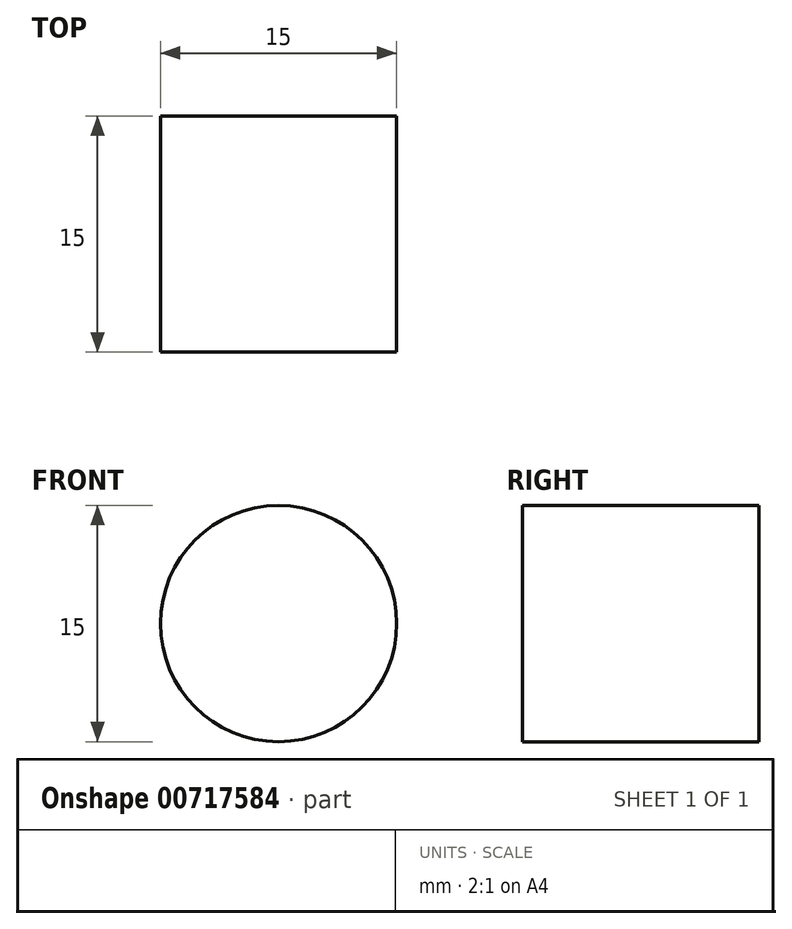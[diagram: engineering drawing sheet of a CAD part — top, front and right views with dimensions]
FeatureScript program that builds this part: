
annotation { "Feature Type Name" : "Feature", "Feature Type Description" : "" }
export const myFeature = defineFeature(function(context is Context, id is Id, definition is map)
    precondition{}
    {
        {
            var Q0;
            Q0=qCreatedBy(makeId("Front.planeOp"),FACE);
            var sketch = newSketch(context, id + "F0", { "sketchPlane" : qUnion([Q0])});
            skCircle(sketch, "E0", {"center": v(-22.72, 9.42) * mm, "radius": 7.5 * mm});
            skSolve(sketch);
        }
        {
            var Q0;
            Q0=makeQuery(id+"F0.imprint","IMPRINT",FACE,{"disambiguationData":[TD([[makeQuery(id+"F0.imprint","IMPRINT",EDGE,{"derivedFrom":sQuery(id+"F0.wireOp",EDGE,"E0")}),1.0]])]});
            extrude(context, id + "F1", {"entities" : qUnion([Q0]), "depth" : 15 * mm, "offsetDistance" : 25 * mm});
        }
    });
